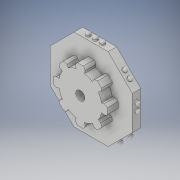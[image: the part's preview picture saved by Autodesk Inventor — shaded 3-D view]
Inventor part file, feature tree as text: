
AUTODESK INVENTOR PART (.ipt)
format: ipt  version: 2017 (Build 210142000, 142)  size: 351,744 bytes
history: native  units: in
note: dims shown in document units (in); Inventor stores cm internally (conversion verified against a paired STEP export)
features: sketch x12, extrude x10, fillet x7, pattern_circular x1
ambient origin geometry x8: Origin, YZ Plane, XZ Plane, XY Plane, X Axis, Y Axis, Z Axis, Center Point
bodies: Solid1 (feature_tree)
feature tree (30):
  extrude  "Extrusion1"  Depth=0.1181in TaperAngle=0.0deg
  extrude  "Extrusion2"  Depth=0.063in
  fillet  "Fillet1"  Radius=0.1in
  sketch  "Sketch3"  dims[d8=0.063in d9=0.063in d10=0.059in]
  sketch  "Sketch4"  dims[d11=0.0472in d12=0.0in d13=0.0315in d24=0.059in]
  sketch  "Sketch5"  dims[d25=0.063in d26=0.1in d27=0.1in d28=0.063in d29=0.063in d31=0.0575in d32=0.059in d34=0.0in d35=0.059in]
  sketch  "Sketch6"  dims[d36=0.059in]
  sketch  "Sketch7"  dims[d40=0.063in d41=0.1in d42=0.1in d43=0.063in d44=0.063in d46=0.059in d47=0.0in d48=0.059in d49=0.059in d50=0.0in d51=0.0in]
  sketch  "Sketch8"  dims[d70=0.063in d71=0.1in d72=0.1in d73=0.063in d74=0.063in d76=0.059in d77=0.0in d78=0.059in d79=0.059in d81=0.0in d82=0.0in]
  sketch  "Sketch9"  dims[d83=0.063in d84=0.1in d85=0.1in d86=0.063in d87=0.063in d89=0.059in d90=0.059in d91=0.059in d92=0.0in d93=0.0in d94=0.0in d95=0.0in]
  extrude  "Extrusion6"  Depth=0.063in
  fillet  "Fillet5"  Radius=0.059in
  extrude  "Extrusion7"  Depth=0.0315in
  fillet  "Fillet6"  Radius=0.059in
  extrude  "Extrusion8"  TaperAngle=0.0deg  [1 undecoded]
  fillet  "Fillet7"  Radius=0.059in
  extrude  "Extrusion9"  TaperAngle=0.0deg  [1 undecoded]
  fillet  "Fillet8"  [1 undecoded]
  extrude  "Extrusion10"  TaperAngle=0.0deg  [1 undecoded]
  fillet  "Fillet9"  [1 undecoded]
  extrude  "Extrusion11"  TaperAngle=0.0deg  [1 undecoded]
  fillet  "Fillet10"  [1 undecoded]
  extrude  "Extrusion14"  Depth=0.0315in
  pattern_circular  "Circular Pattern4"  [2 undecoded]
  extrude  "Extrusion15"  Depth=0.15in TaperAngle=0.0deg
  sketch  "Sketch13"  dims[d125=0.0472in d126=0.0in d127=0.0315in d128=0.0472in d129=0.0in d130=0.0315in d131=0.0472in d132=0.0in d133=0.0315in d134=0.0472in d135=0.0in d136=0.0315in d137=0.0472in d138=0.0in d139=0.0315in d148=0.6in d154=12.5984in d156=360.0deg d161=0.04in d162=0.04in d163=0.15in d164=0.0in d165=3.1496in d166=360.0deg d168=0.075in d169=0.236in d170=0.236in d171=0.236in d172=0.236in d173=0.236in d175=0.236in d176=0.236in d177=0.126in d178=1.0in d179=0.0in]
  sketch  "Sketch1"  dims[d2=0.4724in d3=0.1181in d4=0.0in]
  sketch  "Sketch2"  dims[d5=0.063in d6=0.1in d7=0.1in]
  sketch  "Sketch11"  dims[d96=0.063in d97=0.1in d98=0.1in d99=0.063in d100=0.063in d102=0.059in d103=0.059in d104=0.059in d105=0.0in d106=0.0in d107=0.0in d108=0.0in]
  sketch  "Sketch12"  dims[d109=0.063in d110=0.1in d111=0.1in d112=0.063in d113=0.063in d115=0.059in d116=0.059in d117=0.059in d118=0.0in d119=0.0in d120=0.0in d121=0.0in d122=0.0472in d123=0.0in d124=0.0315in]
note: 9 required parameter values undecoded (feature->parameter linkage not recoverable at this tier; creation-order binding heuristic only, values carry confidence <= 0.55)
